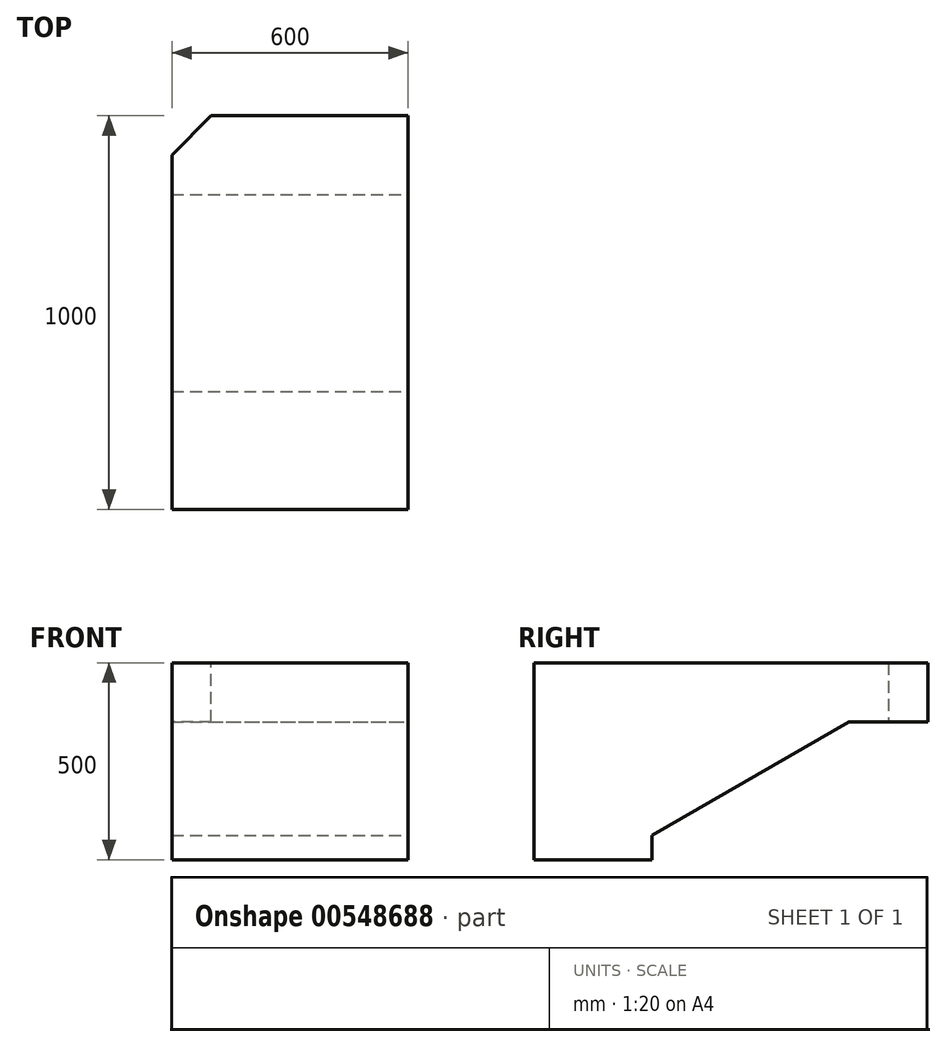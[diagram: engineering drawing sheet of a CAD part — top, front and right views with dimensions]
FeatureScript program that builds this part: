
annotation { "Feature Type Name" : "Feature", "Feature Type Description" : "" }
export const myFeature = defineFeature(function(context is Context, id is Id, definition is map)
    precondition{}
    {
        {
            var Q0;
            Q0=qCreatedBy(makeId("Top.planeOp"),FACE);
            var sketch = newSketch(context, id + "F0", { "sketchPlane" : qUnion([Q0])});
            skLineSegment(sketch, "E0.bottom", {"start": v(-300, -500) * mm, "end": v(300, -500) * mm});
            skLineSegment(sketch, "E0.top", {"start": v(-300, 500) * mm, "end": v(300, 500) * mm});
            skLineSegment(sketch, "E0.left", {"start": v(-300, -500) * mm, "end": v(-300, 500) * mm});
            skLineSegment(sketch, "E0.right", {"start": v(300, -500) * mm, "end": v(300, 500) * mm});
            skPoint(sketch, "E0.middle", {"position": v(0, 0) * mm});
            skSolve(sketch);
        }
        {
            var Q0;
            Q0 = qSketchRegion(id + "F0", true);
            extrude(context, id + "F1", {"entities" : qUnion([Q0]), "depth" : 500 * mm, "offsetDistance" : 25 * mm});
        }
        {
            var Q0;
            Q0=makeQuery(id+"F1.opExtrude","SWEPT_FACE",FACE,{"disambiguationData":[OSD([sQuery(id+"F0.wireOp",EDGE,"E0.right")])]});
            var sketch = newSketch(context, id + "F2", { "sketchPlane" : qUnion([Q0])});
            skLineSegment(sketch, "E1", {"start": v(-200, 0) * mm, "end": v(-200, 61.32) * mm});
            skLineSegment(sketch, "E2", {"start": v(-200, 61.32) * mm, "end": v(300, 350) * mm});
            skLineSegment(sketch, "E3", {"start": v(300, 350) * mm, "end": v(500, 350) * mm});
            skSolve(sketch);
        }
        {
            var Q0;
            {var subQ5=sQuery(id+"F2.wireOp",EDGE,"E1");Q0=makeQuery(id+"F2.imprint","IMPRINT",FACE,{"disambiguationData":[TD([[makeQuery(id+"F2.imprint","IMPRINT",EDGE,{"derivedFrom":subQ5}),-1.0]])]});}
            extrude(context, id + "F3", {"entities" : qUnion([Q0]), "operationType" : NewBodyOperationType.REMOVE, "endBound" : BoundingType.THROUGH_ALL, "oppositeDirection" : true, "depth" : 25 * mm, "offsetDistance" : 25 * mm});
        }
        {
            var Q0;
            Q0=makeQuery(id+"F1.opExtrude","SWEPT_EDGE",EDGE,{"disambiguationData":[OSD([sQuery(id+"F0.wireOp",EDGE,"E0.top"),sQuery(id+"F0.wireOp",EDGE,"E0.left")])]});
            chamfer(context, id + "F4", {"entities" : qUnion([Q0]), "width" : 100 * mm, "tangentPropagation" : true});
        }
    });
